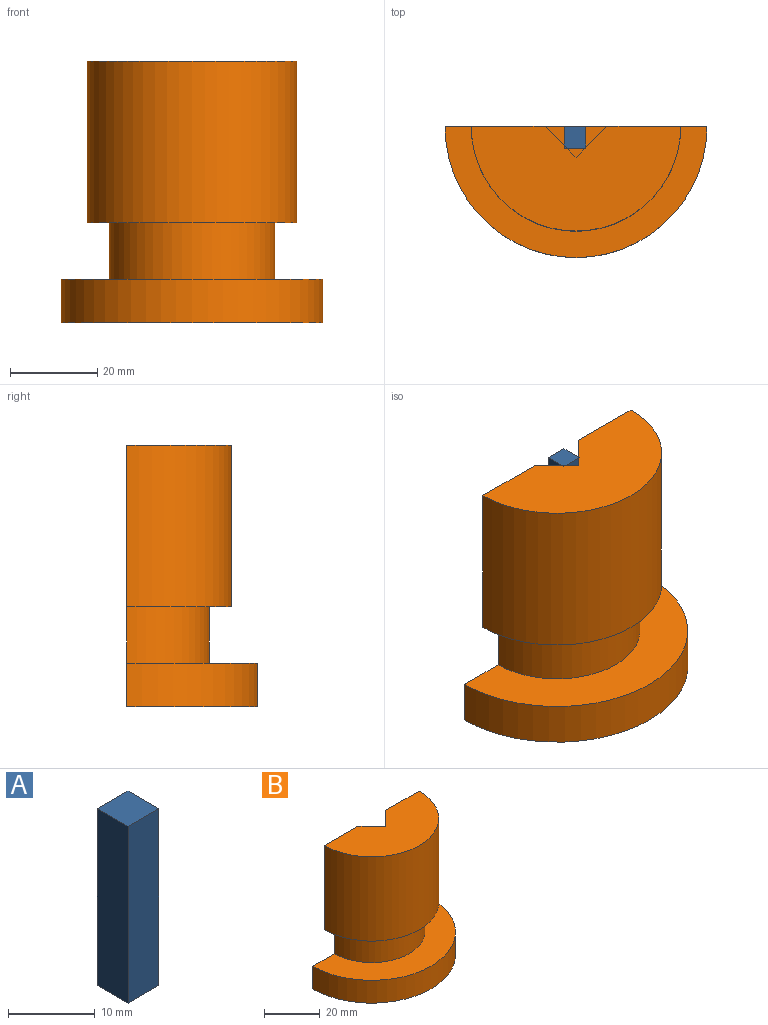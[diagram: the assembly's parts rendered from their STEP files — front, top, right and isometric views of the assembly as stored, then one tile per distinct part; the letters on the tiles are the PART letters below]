
ASSEMBLY  parts=2 mates=2
PART A: 6 faces, bbox 5x5x25 mm
  f0: plane 25x5mm, normal (0,1,0), area 125mm2, adj f1,f3,f4,f5
  f1: plane 25x5mm, normal (-1,0,0), area 125mm2, adj f0,f2,f4,f5
  f2: plane 25x5mm, normal (0,-1,0), area 125mm2, adj f1,f3,f4,f5
  f3: plane 25x5mm, normal (1,0,0), area 125mm2, adj f0,f2,f4,f5
  f4: plane 5x5mm, normal (0,0,1), area 25mm2, adj f0,f1,f2,f3
  f5: plane 5x5mm, normal (0,0,-1), area 25mm2, adj f0,f1,f2,f3
PART B: 11 faces, bbox 60x30x60 mm
  f0: plane 60x60mm, normal (0,1,0), area 2516.4mm2, adj f1,f2,f3,f4,f5,f6,f7,f8
  f1: cylinder r=30mm len=60mm, axis (0,0,-1), area 942.5mm2, adj f0,f2,f7
  f2: plane 60x30mm, normal (0,0,-1), area 1413.7mm2, adj f0,f1
  f3: plane 48x24mm, normal (0,0,1), area 854.8mm2, adj f0,f4,f8,f9
  f4: cylinder r=24mm len=48mm, axis (0,0,-1), area 2789.7mm2, adj f0,f3,f5
  f5: plane 48x24mm, normal (0,0,-1), area 337.7mm2, adj f0,f4,f6
  f6: cylinder r=19mm len=38mm, axis (0,0,-1), area 776mm2, adj f0,f5,f7
  f7: plane 60x30mm, normal (0,0,1), area 846.7mm2, adj f0,f1,f6
  f8: plane 25x7.07mm, normal (0.71,0.71,0), area 250mm2, adj f0,f3,f9,f10
  f9: plane 25x7.07mm, normal (-0.71,0.71,0), area 250mm2, adj f0,f3,f8,f10
  f10: plane 14.14x7.07mm, normal (0,0,1), area 50mm2, adj f0,f8,f9
PLACE A t=(32.06,-43.13,53.51)mm
PLACE B t=(32.29,-40.63,78.51)mm
MATE planar B.f3 <-> A.f4  axis (0,0,1) through (16.76,-40.63,138.51)mm
MATE planar B.f0 <-> A.f0  axis (0,1,0) through (32.29,-40.63,105.56)mm
